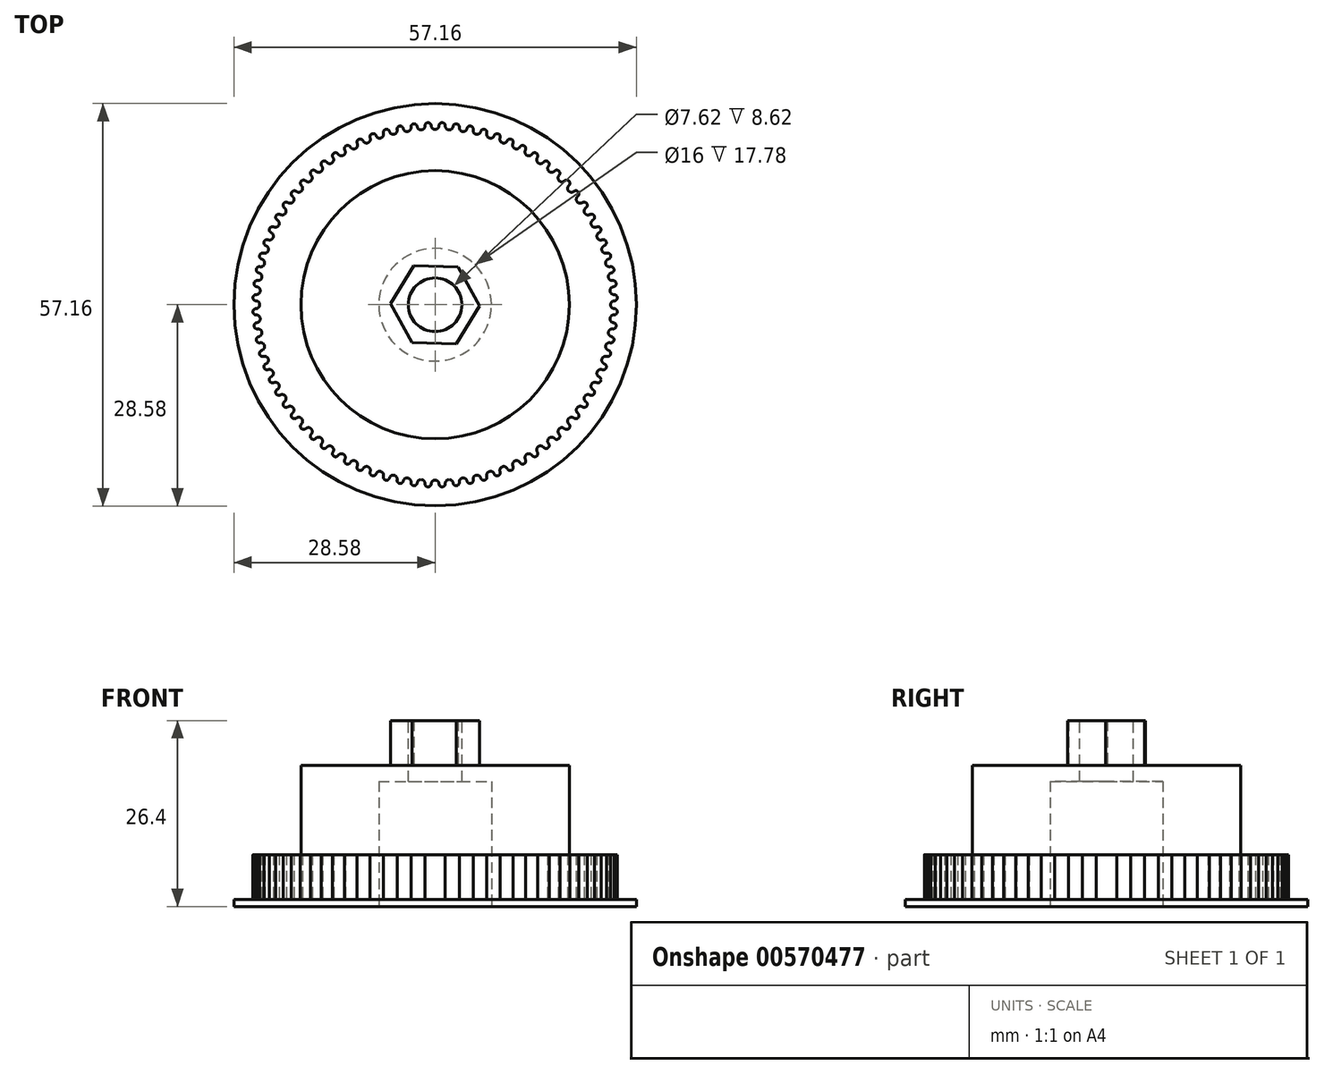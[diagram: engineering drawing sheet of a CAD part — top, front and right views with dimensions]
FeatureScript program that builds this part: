
annotation { "Feature Type Name" : "Feature", "Feature Type Description" : "" }
export const myFeature = defineFeature(function(context is Context, id is Id, definition is map)
    precondition{}
    {
        {
            var Q0;
            Q0=qCreatedBy(makeId("Top.planeOp"),FACE);
            var sketch = newSketch(context, id + "F0", { "sketchPlane" : qUnion([Q0])});
            skCircle(sketch, "E0", {"center": v(0, 0) * mm, "radius": 28.58 * mm});
            skSolve(sketch);
        }
        {
            var Q0;
            Q0 = qSketchRegion(id + "F0", true);
            extrude(context, id + "F1", {"entities" : qUnion([Q0]), "depth" : 1 * mm, "offsetDistance" : 25.4 * mm});
        }
        {
            var Q0;
            Q0=makeQuery(id+"F1.opExtrude","CAP_FACE",FACE,{"disambiguationData":[OSD([sQuery(id+"F0.wireOp",EDGE,"E0")])],"isStart":false});
            var sketch = newSketch(context, id + "F2", { "sketchPlane" : qUnion([Q0])});
            skArc(sketch, "E1", {"start": v(0, 24.9) * mm, "mid": v(-0.98, -24.89) * mm, "end": v(1.95, 24.83) * mm, "construction": true});
            skArc(sketch, "E2", {"start": v(0, 24.9) * mm, "mid": v(0.4, 25.07) * mm, "end": v(0.55, 25.46) * mm});
            skArc(sketch, "E3", {"start": v(1.44, 25.42) * mm, "mid": v(1.58, 25.02) * mm, "end": v(1.95, 24.83) * mm});
            skLineSegment(sketch, "E4", {"start": v(1.95, 24.83) * mm, "end": v(0, 0) * mm, "construction": true});
            skArc(sketch, "E5", {"start": v(1.44, 25.4) * mm, "mid": v(1.02, 25.87) * mm, "end": v(0.55, 25.44) * mm});
            skArc(sketch, "E6.1.0", {"start": v(-0.55, 25.44) * mm, "mid": v(-1.02, 25.87) * mm, "end": v(-1.44, 25.4) * mm});
            skArc(sketch, "E6.1.1", {"start": v(-1.95, 24.83) * mm, "mid": v(-1.58, 25.02) * mm, "end": v(-1.44, 25.42) * mm});
            skArc(sketch, "E6.1.2", {"start": v(-0.55, 25.46) * mm, "mid": v(-0.4, 25.07) * mm, "end": v(0, 24.9) * mm});
            skArc(sketch, "E6.2.0", {"start": v(-2.55, 25.32) * mm, "mid": v(-3.04, 25.7) * mm, "end": v(-3.43, 25.22) * mm});
            skArc(sketch, "E6.2.1", {"start": v(-3.9, 24.6) * mm, "mid": v(-3.54, 24.82) * mm, "end": v(-3.43, 25.23) * mm});
            skArc(sketch, "E6.2.2", {"start": v(-2.55, 25.34) * mm, "mid": v(-2.36, 24.96) * mm, "end": v(-1.95, 24.83) * mm});
            skArc(sketch, "E6.3.0", {"start": v(-4.53, 25.04) * mm, "mid": v(-5.05, 25.4) * mm, "end": v(-5.4, 24.87) * mm});
            skArc(sketch, "E6.3.1", {"start": v(-5.81, 24.22) * mm, "mid": v(-5.47, 24.47) * mm, "end": v(-5.4, 24.88) * mm});
            skArc(sketch, "E6.3.2", {"start": v(-4.53, 25.06) * mm, "mid": v(-4.3, 24.7) * mm, "end": v(-3.9, 24.6) * mm});
            skArc(sketch, "E6.4.0", {"start": v(-6.48, 24.6) * mm, "mid": v(-7.03, 24.92) * mm, "end": v(-7.33, 24.37) * mm});
            skArc(sketch, "E6.4.1", {"start": v(-7.7, 23.69) * mm, "mid": v(-7.38, 23.96) * mm, "end": v(-7.34, 24.38) * mm});
            skArc(sketch, "E6.4.2", {"start": v(-6.48, 24.62) * mm, "mid": v(-6.23, 24.29) * mm, "end": v(-5.81, 24.22) * mm});
            skArc(sketch, "E6.5.0", {"start": v(-8.39, 24.03) * mm, "mid": v(-8.96, 24.29) * mm, "end": v(-9.22, 23.72) * mm});
            skArc(sketch, "E6.5.1", {"start": v(-9.53, 23.01) * mm, "mid": v(-9.23, 23.31) * mm, "end": v(-9.23, 23.73) * mm});
            skArc(sketch, "E6.5.2", {"start": v(-8.4, 24.04) * mm, "mid": v(-8.12, 23.72) * mm, "end": v(-7.7, 23.69) * mm});
            skArc(sketch, "E6.6.0", {"start": v(-10.25, 23.3) * mm, "mid": v(-10.84, 23.51) * mm, "end": v(-11.06, 22.92) * mm});
            skArc(sketch, "E6.6.1", {"start": v(-11.3, 22.2) * mm, "mid": v(-11.03, 22.51) * mm, "end": v(-11.06, 22.93) * mm});
            skArc(sketch, "E6.6.2", {"start": v(-10.25, 23.3) * mm, "mid": v(-9.95, 23.01) * mm, "end": v(-9.53, 23.01) * mm});
            skArc(sketch, "E6.7.0", {"start": v(-12.04, 22.42) * mm, "mid": v(-12.65, 22.59) * mm, "end": v(-12.82, 21.98) * mm});
            skArc(sketch, "E6.7.1", {"start": v(-13.01, 21.24) * mm, "mid": v(-12.77, 21.58) * mm, "end": v(-12.83, 22) * mm});
            skArc(sketch, "E6.7.2", {"start": v(-12.05, 22.43) * mm, "mid": v(-11.73, 22.16) * mm, "end": v(-11.3, 22.2) * mm});
            skArc(sketch, "E6.8.0", {"start": v(-13.77, 21.4) * mm, "mid": v(-14.38, 21.53) * mm, "end": v(-14.5, 20.9) * mm});
            skArc(sketch, "E6.8.1", {"start": v(-14.64, 20.15) * mm, "mid": v(-14.42, 20.51) * mm, "end": v(-14.51, 20.92) * mm});
            skArc(sketch, "E6.8.2", {"start": v(-13.77, 21.42) * mm, "mid": v(-13.43, 21.17) * mm, "end": v(-13.01, 21.24) * mm});
            skArc(sketch, "E6.9.0", {"start": v(-15.4, 20.26) * mm, "mid": v(-16.03, 20.33) * mm, "end": v(-16.1, 19.7) * mm});
            skArc(sketch, "E6.9.1", {"start": v(-16.18, 18.94) * mm, "mid": v(-15.98, 19.32) * mm, "end": v(-16.11, 19.72) * mm});
            skArc(sketch, "E6.9.2", {"start": v(-15.41, 20.27) * mm, "mid": v(-15.05, 20.05) * mm, "end": v(-14.64, 20.15) * mm});
            skArc(sketch, "E6.10.0", {"start": v(-16.94, 18.99) * mm, "mid": v(-17.57, 19.01) * mm, "end": v(-17.6, 18.38) * mm});
            skArc(sketch, "E6.10.1", {"start": v(-17.61, 17.61) * mm, "mid": v(-17.45, 18) * mm, "end": v(-17.6, 18.4) * mm});
            skArc(sketch, "E6.10.2", {"start": v(-16.96, 19) * mm, "mid": v(-16.58, 18.8) * mm, "end": v(-16.18, 18.94) * mm});
            skArc(sketch, "E6.11.0", {"start": v(-18.38, 17.6) * mm, "mid": v(-19.01, 17.57) * mm, "end": v(-18.99, 16.94) * mm});
            skArc(sketch, "E6.11.1", {"start": v(-18.94, 16.18) * mm, "mid": v(-18.8, 16.58) * mm, "end": v(-19, 16.96) * mm});
            skArc(sketch, "E6.11.2", {"start": v(-18.4, 17.6) * mm, "mid": v(-18, 17.45) * mm, "end": v(-17.61, 17.61) * mm});
            skArc(sketch, "E6.12.0", {"start": v(-19.7, 16.1) * mm, "mid": v(-20.33, 16.03) * mm, "end": v(-20.26, 15.4) * mm});
            skArc(sketch, "E6.12.1", {"start": v(-20.15, 14.64) * mm, "mid": v(-20.05, 15.05) * mm, "end": v(-20.27, 15.41) * mm});
            skArc(sketch, "E6.12.2", {"start": v(-19.72, 16.11) * mm, "mid": v(-19.32, 15.98) * mm, "end": v(-18.94, 16.18) * mm});
            skArc(sketch, "E6.13.0", {"start": v(-20.9, 14.5) * mm, "mid": v(-21.53, 14.38) * mm, "end": v(-21.4, 13.77) * mm});
            skArc(sketch, "E6.13.1", {"start": v(-21.24, 13.01) * mm, "mid": v(-21.17, 13.43) * mm, "end": v(-21.42, 13.77) * mm});
            skArc(sketch, "E6.13.2", {"start": v(-20.92, 14.51) * mm, "mid": v(-20.51, 14.42) * mm, "end": v(-20.15, 14.64) * mm});
            skArc(sketch, "E6.14.0", {"start": v(-21.98, 12.82) * mm, "mid": v(-22.59, 12.65) * mm, "end": v(-22.42, 12.04) * mm});
            skArc(sketch, "E6.14.1", {"start": v(-22.2, 11.3) * mm, "mid": v(-22.16, 11.73) * mm, "end": v(-22.43, 12.05) * mm});
            skArc(sketch, "E6.14.2", {"start": v(-22, 12.83) * mm, "mid": v(-21.58, 12.77) * mm, "end": v(-21.24, 13.01) * mm});
            skArc(sketch, "E6.15.0", {"start": v(-22.92, 11.06) * mm, "mid": v(-23.51, 10.84) * mm, "end": v(-23.3, 10.25) * mm});
            skArc(sketch, "E6.15.1", {"start": v(-23.01, 9.53) * mm, "mid": v(-23.01, 9.95) * mm, "end": v(-23.3, 10.25) * mm});
            skArc(sketch, "E6.15.2", {"start": v(-22.93, 11.06) * mm, "mid": v(-22.51, 11.03) * mm, "end": v(-22.2, 11.3) * mm});
            skArc(sketch, "E6.16.0", {"start": v(-23.72, 9.22) * mm, "mid": v(-24.29, 8.96) * mm, "end": v(-24.03, 8.39) * mm});
            skArc(sketch, "E6.16.1", {"start": v(-23.69, 7.7) * mm, "mid": v(-23.72, 8.12) * mm, "end": v(-24.04, 8.4) * mm});
            skArc(sketch, "E6.16.2", {"start": v(-23.73, 9.23) * mm, "mid": v(-23.31, 9.23) * mm, "end": v(-23.01, 9.53) * mm});
            skArc(sketch, "E6.17.0", {"start": v(-24.37, 7.33) * mm, "mid": v(-24.92, 7.03) * mm, "end": v(-24.6, 6.48) * mm});
            skArc(sketch, "E6.17.1", {"start": v(-24.22, 5.81) * mm, "mid": v(-24.29, 6.23) * mm, "end": v(-24.62, 6.48) * mm});
            skArc(sketch, "E6.17.2", {"start": v(-24.38, 7.34) * mm, "mid": v(-23.96, 7.38) * mm, "end": v(-23.69, 7.7) * mm});
            skArc(sketch, "E6.18.0", {"start": v(-24.87, 5.4) * mm, "mid": v(-25.4, 5.05) * mm, "end": v(-25.04, 4.53) * mm});
            skArc(sketch, "E6.18.1", {"start": v(-24.6, 3.9) * mm, "mid": v(-24.7, 4.3) * mm, "end": v(-25.06, 4.53) * mm});
            skArc(sketch, "E6.18.2", {"start": v(-24.88, 5.4) * mm, "mid": v(-24.47, 5.47) * mm, "end": v(-24.22, 5.81) * mm});
            skArc(sketch, "E6.19.0", {"start": v(-25.22, 3.43) * mm, "mid": v(-25.7, 3.04) * mm, "end": v(-25.32, 2.55) * mm});
            skArc(sketch, "E6.19.1", {"start": v(-24.83, 1.95) * mm, "mid": v(-24.96, 2.36) * mm, "end": v(-25.34, 2.55) * mm});
            skArc(sketch, "E6.19.2", {"start": v(-25.23, 3.43) * mm, "mid": v(-24.82, 3.54) * mm, "end": v(-24.6, 3.9) * mm});
            skArc(sketch, "E6.20.0", {"start": v(-25.4, 1.44) * mm, "mid": v(-25.87, 1.02) * mm, "end": v(-25.44, 0.55) * mm});
            skArc(sketch, "E6.20.1", {"start": v(-24.9, 0) * mm, "mid": v(-25.07, 0.4) * mm, "end": v(-25.46, 0.55) * mm});
            skArc(sketch, "E6.20.2", {"start": v(-25.42, 1.44) * mm, "mid": v(-25.02, 1.58) * mm, "end": v(-24.83, 1.95) * mm});
            skArc(sketch, "E6.21.0", {"start": v(-25.44, -0.55) * mm, "mid": v(-25.87, -1.02) * mm, "end": v(-25.4, -1.44) * mm});
            skArc(sketch, "E6.21.1", {"start": v(-24.83, -1.95) * mm, "mid": v(-25.02, -1.58) * mm, "end": v(-25.42, -1.44) * mm});
            skArc(sketch, "E6.21.2", {"start": v(-25.46, -0.55) * mm, "mid": v(-25.07, -0.4) * mm, "end": v(-24.9, 0) * mm});
            skArc(sketch, "E6.22.0", {"start": v(-25.32, -2.55) * mm, "mid": v(-25.7, -3.04) * mm, "end": v(-25.22, -3.43) * mm});
            skArc(sketch, "E6.22.1", {"start": v(-24.6, -3.9) * mm, "mid": v(-24.82, -3.54) * mm, "end": v(-25.23, -3.43) * mm});
            skArc(sketch, "E6.22.2", {"start": v(-25.34, -2.55) * mm, "mid": v(-24.96, -2.36) * mm, "end": v(-24.83, -1.95) * mm});
            skArc(sketch, "E6.23.0", {"start": v(-25.04, -4.53) * mm, "mid": v(-25.4, -5.05) * mm, "end": v(-24.87, -5.4) * mm});
            skArc(sketch, "E6.23.1", {"start": v(-24.22, -5.81) * mm, "mid": v(-24.47, -5.47) * mm, "end": v(-24.88, -5.4) * mm});
            skArc(sketch, "E6.23.2", {"start": v(-25.06, -4.53) * mm, "mid": v(-24.7, -4.3) * mm, "end": v(-24.6, -3.9) * mm});
            skArc(sketch, "E6.24.0", {"start": v(-24.6, -6.48) * mm, "mid": v(-24.92, -7.03) * mm, "end": v(-24.37, -7.33) * mm});
            skArc(sketch, "E6.24.1", {"start": v(-23.69, -7.7) * mm, "mid": v(-23.96, -7.38) * mm, "end": v(-24.38, -7.34) * mm});
            skArc(sketch, "E6.24.2", {"start": v(-24.62, -6.48) * mm, "mid": v(-24.29, -6.23) * mm, "end": v(-24.22, -5.81) * mm});
            skArc(sketch, "E6.25.0", {"start": v(-24.03, -8.39) * mm, "mid": v(-24.29, -8.96) * mm, "end": v(-23.72, -9.22) * mm});
            skArc(sketch, "E6.25.1", {"start": v(-23.01, -9.53) * mm, "mid": v(-23.31, -9.23) * mm, "end": v(-23.73, -9.23) * mm});
            skArc(sketch, "E6.25.2", {"start": v(-24.04, -8.4) * mm, "mid": v(-23.72, -8.12) * mm, "end": v(-23.69, -7.7) * mm});
            skArc(sketch, "E6.26.0", {"start": v(-23.3, -10.25) * mm, "mid": v(-23.51, -10.84) * mm, "end": v(-22.92, -11.06) * mm});
            skArc(sketch, "E6.26.1", {"start": v(-22.2, -11.3) * mm, "mid": v(-22.51, -11.03) * mm, "end": v(-22.93, -11.06) * mm});
            skArc(sketch, "E6.26.2", {"start": v(-23.3, -10.25) * mm, "mid": v(-23.01, -9.95) * mm, "end": v(-23.01, -9.53) * mm});
            skArc(sketch, "E6.27.0", {"start": v(-22.42, -12.04) * mm, "mid": v(-22.59, -12.65) * mm, "end": v(-21.98, -12.82) * mm});
            skArc(sketch, "E6.27.1", {"start": v(-21.24, -13.01) * mm, "mid": v(-21.58, -12.77) * mm, "end": v(-22, -12.83) * mm});
            skArc(sketch, "E6.27.2", {"start": v(-22.43, -12.05) * mm, "mid": v(-22.16, -11.73) * mm, "end": v(-22.2, -11.3) * mm});
            skArc(sketch, "E6.28.0", {"start": v(-21.4, -13.77) * mm, "mid": v(-21.53, -14.38) * mm, "end": v(-20.9, -14.5) * mm});
            skArc(sketch, "E6.28.1", {"start": v(-20.15, -14.64) * mm, "mid": v(-20.51, -14.42) * mm, "end": v(-20.92, -14.51) * mm});
            skArc(sketch, "E6.28.2", {"start": v(-21.42, -13.77) * mm, "mid": v(-21.17, -13.43) * mm, "end": v(-21.24, -13.01) * mm});
            skArc(sketch, "E6.29.0", {"start": v(-20.26, -15.4) * mm, "mid": v(-20.33, -16.03) * mm, "end": v(-19.7, -16.1) * mm});
            skArc(sketch, "E6.29.1", {"start": v(-18.94, -16.18) * mm, "mid": v(-19.32, -15.98) * mm, "end": v(-19.72, -16.11) * mm});
            skArc(sketch, "E6.29.2", {"start": v(-20.27, -15.41) * mm, "mid": v(-20.05, -15.05) * mm, "end": v(-20.15, -14.64) * mm});
            skArc(sketch, "E6.30.0", {"start": v(-18.99, -16.94) * mm, "mid": v(-19.01, -17.57) * mm, "end": v(-18.38, -17.6) * mm});
            skArc(sketch, "E6.30.1", {"start": v(-17.61, -17.61) * mm, "mid": v(-18, -17.45) * mm, "end": v(-18.4, -17.6) * mm});
            skArc(sketch, "E6.30.2", {"start": v(-19, -16.96) * mm, "mid": v(-18.8, -16.58) * mm, "end": v(-18.94, -16.18) * mm});
            skArc(sketch, "E6.31.0", {"start": v(-17.6, -18.38) * mm, "mid": v(-17.57, -19.01) * mm, "end": v(-16.94, -18.99) * mm});
            skArc(sketch, "E6.31.1", {"start": v(-16.18, -18.94) * mm, "mid": v(-16.58, -18.8) * mm, "end": v(-16.96, -19) * mm});
            skArc(sketch, "E6.31.2", {"start": v(-17.6, -18.4) * mm, "mid": v(-17.45, -18) * mm, "end": v(-17.61, -17.61) * mm});
            skArc(sketch, "E6.32.0", {"start": v(-16.1, -19.7) * mm, "mid": v(-16.03, -20.33) * mm, "end": v(-15.4, -20.26) * mm});
            skArc(sketch, "E6.32.1", {"start": v(-14.64, -20.15) * mm, "mid": v(-15.05, -20.05) * mm, "end": v(-15.41, -20.27) * mm});
            skArc(sketch, "E6.32.2", {"start": v(-16.11, -19.72) * mm, "mid": v(-15.98, -19.32) * mm, "end": v(-16.18, -18.94) * mm});
            skArc(sketch, "E6.33.0", {"start": v(-14.5, -20.9) * mm, "mid": v(-14.38, -21.53) * mm, "end": v(-13.77, -21.4) * mm});
            skArc(sketch, "E6.33.1", {"start": v(-13.01, -21.24) * mm, "mid": v(-13.43, -21.17) * mm, "end": v(-13.77, -21.42) * mm});
            skArc(sketch, "E6.33.2", {"start": v(-14.51, -20.92) * mm, "mid": v(-14.42, -20.51) * mm, "end": v(-14.64, -20.15) * mm});
            skArc(sketch, "E6.34.0", {"start": v(-12.82, -21.98) * mm, "mid": v(-12.65, -22.59) * mm, "end": v(-12.04, -22.42) * mm});
            skArc(sketch, "E6.34.1", {"start": v(-11.3, -22.2) * mm, "mid": v(-11.73, -22.16) * mm, "end": v(-12.05, -22.43) * mm});
            skArc(sketch, "E6.34.2", {"start": v(-12.83, -22) * mm, "mid": v(-12.77, -21.58) * mm, "end": v(-13.01, -21.24) * mm});
            skArc(sketch, "E6.35.0", {"start": v(-11.06, -22.92) * mm, "mid": v(-10.84, -23.51) * mm, "end": v(-10.25, -23.3) * mm});
            skArc(sketch, "E6.35.1", {"start": v(-9.53, -23.01) * mm, "mid": v(-9.95, -23.01) * mm, "end": v(-10.25, -23.3) * mm});
            skArc(sketch, "E6.35.2", {"start": v(-11.06, -22.93) * mm, "mid": v(-11.03, -22.51) * mm, "end": v(-11.3, -22.2) * mm});
            skArc(sketch, "E6.36.0", {"start": v(-9.22, -23.72) * mm, "mid": v(-8.96, -24.29) * mm, "end": v(-8.39, -24.03) * mm});
            skArc(sketch, "E6.36.1", {"start": v(-7.7, -23.69) * mm, "mid": v(-8.12, -23.72) * mm, "end": v(-8.4, -24.04) * mm});
            skArc(sketch, "E6.36.2", {"start": v(-9.23, -23.73) * mm, "mid": v(-9.23, -23.31) * mm, "end": v(-9.53, -23.01) * mm});
            skArc(sketch, "E6.37.0", {"start": v(-7.33, -24.37) * mm, "mid": v(-7.03, -24.92) * mm, "end": v(-6.48, -24.6) * mm});
            skArc(sketch, "E6.37.1", {"start": v(-5.81, -24.22) * mm, "mid": v(-6.23, -24.29) * mm, "end": v(-6.48, -24.62) * mm});
            skArc(sketch, "E6.37.2", {"start": v(-7.34, -24.38) * mm, "mid": v(-7.38, -23.96) * mm, "end": v(-7.7, -23.69) * mm});
            skArc(sketch, "E6.38.0", {"start": v(-5.4, -24.87) * mm, "mid": v(-5.05, -25.4) * mm, "end": v(-4.53, -25.04) * mm});
            skArc(sketch, "E6.38.1", {"start": v(-3.9, -24.6) * mm, "mid": v(-4.3, -24.7) * mm, "end": v(-4.53, -25.06) * mm});
            skArc(sketch, "E6.38.2", {"start": v(-5.4, -24.88) * mm, "mid": v(-5.47, -24.47) * mm, "end": v(-5.81, -24.22) * mm});
            skArc(sketch, "E6.39.0", {"start": v(-3.43, -25.22) * mm, "mid": v(-3.04, -25.7) * mm, "end": v(-2.55, -25.32) * mm});
            skArc(sketch, "E6.39.1", {"start": v(-1.95, -24.83) * mm, "mid": v(-2.36, -24.96) * mm, "end": v(-2.55, -25.34) * mm});
            skArc(sketch, "E6.39.2", {"start": v(-3.43, -25.23) * mm, "mid": v(-3.54, -24.82) * mm, "end": v(-3.9, -24.6) * mm});
            skArc(sketch, "E6.40.0", {"start": v(-1.44, -25.4) * mm, "mid": v(-1.02, -25.87) * mm, "end": v(-0.55, -25.44) * mm});
            skArc(sketch, "E6.40.1", {"start": v(0, -24.9) * mm, "mid": v(-0.4, -25.07) * mm, "end": v(-0.55, -25.46) * mm});
            skArc(sketch, "E6.40.2", {"start": v(-1.44, -25.42) * mm, "mid": v(-1.58, -25.02) * mm, "end": v(-1.95, -24.83) * mm});
            skArc(sketch, "E6.41.0", {"start": v(0.55, -25.44) * mm, "mid": v(1.02, -25.87) * mm, "end": v(1.44, -25.4) * mm});
            skArc(sketch, "E6.41.1", {"start": v(1.95, -24.83) * mm, "mid": v(1.58, -25.02) * mm, "end": v(1.44, -25.42) * mm});
            skArc(sketch, "E6.41.2", {"start": v(0.55, -25.46) * mm, "mid": v(0.4, -25.07) * mm, "end": v(0, -24.9) * mm});
            skArc(sketch, "E6.42.0", {"start": v(2.55, -25.32) * mm, "mid": v(3.04, -25.7) * mm, "end": v(3.43, -25.22) * mm});
            skArc(sketch, "E6.42.1", {"start": v(3.9, -24.6) * mm, "mid": v(3.54, -24.82) * mm, "end": v(3.43, -25.23) * mm});
            skArc(sketch, "E6.42.2", {"start": v(2.55, -25.34) * mm, "mid": v(2.36, -24.96) * mm, "end": v(1.95, -24.83) * mm});
            skArc(sketch, "E6.43.0", {"start": v(4.53, -25.04) * mm, "mid": v(5.05, -25.4) * mm, "end": v(5.4, -24.87) * mm});
            skArc(sketch, "E6.43.1", {"start": v(5.81, -24.22) * mm, "mid": v(5.47, -24.47) * mm, "end": v(5.4, -24.88) * mm});
            skArc(sketch, "E6.43.2", {"start": v(4.53, -25.06) * mm, "mid": v(4.3, -24.7) * mm, "end": v(3.9, -24.6) * mm});
            skArc(sketch, "E6.44.0", {"start": v(6.48, -24.6) * mm, "mid": v(7.03, -24.92) * mm, "end": v(7.33, -24.37) * mm});
            skArc(sketch, "E6.44.1", {"start": v(7.7, -23.69) * mm, "mid": v(7.38, -23.96) * mm, "end": v(7.34, -24.38) * mm});
            skArc(sketch, "E6.44.2", {"start": v(6.48, -24.62) * mm, "mid": v(6.23, -24.29) * mm, "end": v(5.81, -24.22) * mm});
            skArc(sketch, "E6.45.0", {"start": v(8.39, -24.03) * mm, "mid": v(8.96, -24.29) * mm, "end": v(9.22, -23.72) * mm});
            skArc(sketch, "E6.45.1", {"start": v(9.53, -23.01) * mm, "mid": v(9.23, -23.31) * mm, "end": v(9.23, -23.73) * mm});
            skArc(sketch, "E6.45.2", {"start": v(8.4, -24.04) * mm, "mid": v(8.12, -23.72) * mm, "end": v(7.7, -23.69) * mm});
            skArc(sketch, "E6.46.0", {"start": v(10.25, -23.3) * mm, "mid": v(10.84, -23.51) * mm, "end": v(11.06, -22.92) * mm});
            skArc(sketch, "E6.46.1", {"start": v(11.3, -22.2) * mm, "mid": v(11.03, -22.51) * mm, "end": v(11.06, -22.93) * mm});
            skArc(sketch, "E6.46.2", {"start": v(10.25, -23.3) * mm, "mid": v(9.95, -23.01) * mm, "end": v(9.53, -23.01) * mm});
            skArc(sketch, "E6.47.0", {"start": v(12.04, -22.42) * mm, "mid": v(12.65, -22.59) * mm, "end": v(12.82, -21.98) * mm});
            skArc(sketch, "E6.47.1", {"start": v(13.01, -21.24) * mm, "mid": v(12.77, -21.58) * mm, "end": v(12.83, -22) * mm});
            skArc(sketch, "E6.47.2", {"start": v(12.05, -22.43) * mm, "mid": v(11.73, -22.16) * mm, "end": v(11.3, -22.2) * mm});
            skArc(sketch, "E6.48.0", {"start": v(13.77, -21.4) * mm, "mid": v(14.38, -21.53) * mm, "end": v(14.5, -20.9) * mm});
            skArc(sketch, "E6.48.1", {"start": v(14.64, -20.15) * mm, "mid": v(14.42, -20.51) * mm, "end": v(14.51, -20.92) * mm});
            skArc(sketch, "E6.48.2", {"start": v(13.77, -21.42) * mm, "mid": v(13.43, -21.17) * mm, "end": v(13.01, -21.24) * mm});
            skArc(sketch, "E6.49.0", {"start": v(15.4, -20.26) * mm, "mid": v(16.03, -20.33) * mm, "end": v(16.1, -19.7) * mm});
            skArc(sketch, "E6.49.1", {"start": v(16.18, -18.94) * mm, "mid": v(15.98, -19.32) * mm, "end": v(16.11, -19.72) * mm});
            skArc(sketch, "E6.49.2", {"start": v(15.41, -20.27) * mm, "mid": v(15.05, -20.05) * mm, "end": v(14.64, -20.15) * mm});
            skArc(sketch, "E6.50.0", {"start": v(16.94, -18.99) * mm, "mid": v(17.57, -19.01) * mm, "end": v(17.6, -18.38) * mm});
            skArc(sketch, "E6.50.1", {"start": v(17.61, -17.61) * mm, "mid": v(17.45, -18) * mm, "end": v(17.6, -18.4) * mm});
            skArc(sketch, "E6.50.2", {"start": v(16.96, -19) * mm, "mid": v(16.58, -18.8) * mm, "end": v(16.18, -18.94) * mm});
            skArc(sketch, "E6.51.0", {"start": v(18.38, -17.6) * mm, "mid": v(19.01, -17.57) * mm, "end": v(18.99, -16.94) * mm});
            skArc(sketch, "E6.51.1", {"start": v(18.94, -16.18) * mm, "mid": v(18.8, -16.58) * mm, "end": v(19, -16.96) * mm});
            skArc(sketch, "E6.51.2", {"start": v(18.4, -17.6) * mm, "mid": v(18, -17.45) * mm, "end": v(17.61, -17.61) * mm});
            skArc(sketch, "E6.52.0", {"start": v(19.7, -16.1) * mm, "mid": v(20.33, -16.03) * mm, "end": v(20.26, -15.4) * mm});
            skArc(sketch, "E6.52.1", {"start": v(20.15, -14.64) * mm, "mid": v(20.05, -15.05) * mm, "end": v(20.27, -15.41) * mm});
            skArc(sketch, "E6.52.2", {"start": v(19.72, -16.11) * mm, "mid": v(19.32, -15.98) * mm, "end": v(18.94, -16.18) * mm});
            skArc(sketch, "E6.53.0", {"start": v(20.9, -14.5) * mm, "mid": v(21.53, -14.38) * mm, "end": v(21.4, -13.77) * mm});
            skArc(sketch, "E6.53.1", {"start": v(21.24, -13.01) * mm, "mid": v(21.17, -13.43) * mm, "end": v(21.42, -13.77) * mm});
            skArc(sketch, "E6.53.2", {"start": v(20.92, -14.51) * mm, "mid": v(20.51, -14.42) * mm, "end": v(20.15, -14.64) * mm});
            skArc(sketch, "E6.54.0", {"start": v(21.98, -12.82) * mm, "mid": v(22.59, -12.65) * mm, "end": v(22.42, -12.04) * mm});
            skArc(sketch, "E6.54.1", {"start": v(22.2, -11.3) * mm, "mid": v(22.16, -11.73) * mm, "end": v(22.43, -12.05) * mm});
            skArc(sketch, "E6.54.2", {"start": v(22, -12.83) * mm, "mid": v(21.58, -12.77) * mm, "end": v(21.24, -13.01) * mm});
            skArc(sketch, "E6.55.0", {"start": v(22.92, -11.06) * mm, "mid": v(23.51, -10.84) * mm, "end": v(23.3, -10.25) * mm});
            skArc(sketch, "E6.55.1", {"start": v(23.01, -9.53) * mm, "mid": v(23.01, -9.95) * mm, "end": v(23.3, -10.25) * mm});
            skArc(sketch, "E6.55.2", {"start": v(22.93, -11.06) * mm, "mid": v(22.51, -11.03) * mm, "end": v(22.2, -11.3) * mm});
            skArc(sketch, "E6.56.0", {"start": v(23.72, -9.22) * mm, "mid": v(24.29, -8.96) * mm, "end": v(24.03, -8.39) * mm});
            skArc(sketch, "E6.56.1", {"start": v(23.69, -7.7) * mm, "mid": v(23.72, -8.12) * mm, "end": v(24.04, -8.4) * mm});
            skArc(sketch, "E6.56.2", {"start": v(23.73, -9.23) * mm, "mid": v(23.31, -9.23) * mm, "end": v(23.01, -9.53) * mm});
            skArc(sketch, "E6.57.0", {"start": v(24.37, -7.33) * mm, "mid": v(24.92, -7.03) * mm, "end": v(24.6, -6.48) * mm});
            skArc(sketch, "E6.57.1", {"start": v(24.22, -5.81) * mm, "mid": v(24.29, -6.23) * mm, "end": v(24.62, -6.48) * mm});
            skArc(sketch, "E6.57.2", {"start": v(24.38, -7.34) * mm, "mid": v(23.96, -7.38) * mm, "end": v(23.69, -7.7) * mm});
            skArc(sketch, "E6.58.0", {"start": v(24.87, -5.4) * mm, "mid": v(25.4, -5.05) * mm, "end": v(25.04, -4.53) * mm});
            skArc(sketch, "E6.58.1", {"start": v(24.6, -3.9) * mm, "mid": v(24.7, -4.3) * mm, "end": v(25.06, -4.53) * mm});
            skArc(sketch, "E6.58.2", {"start": v(24.88, -5.4) * mm, "mid": v(24.47, -5.47) * mm, "end": v(24.22, -5.81) * mm});
            skArc(sketch, "E6.59.0", {"start": v(25.22, -3.43) * mm, "mid": v(25.7, -3.04) * mm, "end": v(25.32, -2.55) * mm});
            skArc(sketch, "E6.59.1", {"start": v(24.83, -1.95) * mm, "mid": v(24.96, -2.36) * mm, "end": v(25.34, -2.55) * mm});
            skArc(sketch, "E6.59.2", {"start": v(25.23, -3.43) * mm, "mid": v(24.82, -3.54) * mm, "end": v(24.6, -3.9) * mm});
            skArc(sketch, "E6.60.0", {"start": v(25.4, -1.44) * mm, "mid": v(25.87, -1.02) * mm, "end": v(25.44, -0.55) * mm});
            skArc(sketch, "E6.60.1", {"start": v(24.9, 0) * mm, "mid": v(25.07, -0.4) * mm, "end": v(25.46, -0.55) * mm});
            skArc(sketch, "E6.60.2", {"start": v(25.42, -1.44) * mm, "mid": v(25.02, -1.58) * mm, "end": v(24.83, -1.95) * mm});
            skArc(sketch, "E6.61.0", {"start": v(25.44, 0.55) * mm, "mid": v(25.87, 1.02) * mm, "end": v(25.4, 1.44) * mm});
            skArc(sketch, "E6.61.1", {"start": v(24.83, 1.95) * mm, "mid": v(25.02, 1.58) * mm, "end": v(25.42, 1.44) * mm});
            skArc(sketch, "E6.61.2", {"start": v(25.46, 0.55) * mm, "mid": v(25.07, 0.4) * mm, "end": v(24.9, 0) * mm});
            skArc(sketch, "E6.62.0", {"start": v(25.32, 2.55) * mm, "mid": v(25.7, 3.04) * mm, "end": v(25.22, 3.43) * mm});
            skArc(sketch, "E6.62.1", {"start": v(24.6, 3.9) * mm, "mid": v(24.82, 3.54) * mm, "end": v(25.23, 3.43) * mm});
            skArc(sketch, "E6.62.2", {"start": v(25.34, 2.55) * mm, "mid": v(24.96, 2.36) * mm, "end": v(24.83, 1.95) * mm});
            skArc(sketch, "E6.63.0", {"start": v(25.04, 4.53) * mm, "mid": v(25.4, 5.05) * mm, "end": v(24.87, 5.4) * mm});
            skArc(sketch, "E6.63.1", {"start": v(24.22, 5.81) * mm, "mid": v(24.47, 5.47) * mm, "end": v(24.88, 5.4) * mm});
            skArc(sketch, "E6.63.2", {"start": v(25.06, 4.53) * mm, "mid": v(24.7, 4.3) * mm, "end": v(24.6, 3.9) * mm});
            skArc(sketch, "E6.64.0", {"start": v(24.6, 6.48) * mm, "mid": v(24.92, 7.03) * mm, "end": v(24.37, 7.33) * mm});
            skArc(sketch, "E6.64.1", {"start": v(23.69, 7.7) * mm, "mid": v(23.96, 7.38) * mm, "end": v(24.38, 7.34) * mm});
            skArc(sketch, "E6.64.2", {"start": v(24.62, 6.48) * mm, "mid": v(24.29, 6.23) * mm, "end": v(24.22, 5.81) * mm});
            skArc(sketch, "E6.65.0", {"start": v(24.03, 8.39) * mm, "mid": v(24.29, 8.96) * mm, "end": v(23.72, 9.22) * mm});
            skArc(sketch, "E6.65.1", {"start": v(23.01, 9.53) * mm, "mid": v(23.31, 9.23) * mm, "end": v(23.73, 9.23) * mm});
            skArc(sketch, "E6.65.2", {"start": v(24.04, 8.4) * mm, "mid": v(23.72, 8.12) * mm, "end": v(23.69, 7.7) * mm});
            skArc(sketch, "E6.66.0", {"start": v(23.3, 10.25) * mm, "mid": v(23.51, 10.84) * mm, "end": v(22.92, 11.06) * mm});
            skArc(sketch, "E6.66.1", {"start": v(22.2, 11.3) * mm, "mid": v(22.51, 11.03) * mm, "end": v(22.93, 11.06) * mm});
            skArc(sketch, "E6.66.2", {"start": v(23.3, 10.25) * mm, "mid": v(23.01, 9.95) * mm, "end": v(23.01, 9.53) * mm});
            skArc(sketch, "E6.67.0", {"start": v(22.42, 12.04) * mm, "mid": v(22.59, 12.65) * mm, "end": v(21.98, 12.82) * mm});
            skArc(sketch, "E6.67.1", {"start": v(21.24, 13.01) * mm, "mid": v(21.58, 12.77) * mm, "end": v(22, 12.83) * mm});
            skArc(sketch, "E6.67.2", {"start": v(22.43, 12.05) * mm, "mid": v(22.16, 11.73) * mm, "end": v(22.2, 11.3) * mm});
            skArc(sketch, "E6.68.0", {"start": v(21.4, 13.77) * mm, "mid": v(21.53, 14.38) * mm, "end": v(20.9, 14.5) * mm});
            skArc(sketch, "E6.68.1", {"start": v(20.15, 14.64) * mm, "mid": v(20.51, 14.42) * mm, "end": v(20.92, 14.51) * mm});
            skArc(sketch, "E6.68.2", {"start": v(21.42, 13.77) * mm, "mid": v(21.17, 13.43) * mm, "end": v(21.24, 13.01) * mm});
            skArc(sketch, "E6.69.0", {"start": v(20.26, 15.4) * mm, "mid": v(20.33, 16.03) * mm, "end": v(19.7, 16.1) * mm});
            skArc(sketch, "E6.69.1", {"start": v(18.94, 16.18) * mm, "mid": v(19.32, 15.98) * mm, "end": v(19.72, 16.11) * mm});
            skArc(sketch, "E6.69.2", {"start": v(20.27, 15.41) * mm, "mid": v(20.05, 15.05) * mm, "end": v(20.15, 14.64) * mm});
            skArc(sketch, "E6.70.0", {"start": v(18.99, 16.94) * mm, "mid": v(19.01, 17.57) * mm, "end": v(18.38, 17.6) * mm});
            skArc(sketch, "E6.70.1", {"start": v(17.61, 17.61) * mm, "mid": v(18, 17.45) * mm, "end": v(18.4, 17.6) * mm});
            skArc(sketch, "E6.70.2", {"start": v(19, 16.96) * mm, "mid": v(18.8, 16.58) * mm, "end": v(18.94, 16.18) * mm});
            skArc(sketch, "E6.71.0", {"start": v(17.6, 18.38) * mm, "mid": v(17.57, 19.01) * mm, "end": v(16.94, 18.99) * mm});
            skArc(sketch, "E6.71.1", {"start": v(16.18, 18.94) * mm, "mid": v(16.58, 18.8) * mm, "end": v(16.96, 19) * mm});
            skArc(sketch, "E6.71.2", {"start": v(17.6, 18.4) * mm, "mid": v(17.45, 18) * mm, "end": v(17.61, 17.61) * mm});
            skArc(sketch, "E6.72.0", {"start": v(16.1, 19.7) * mm, "mid": v(16.03, 20.33) * mm, "end": v(15.4, 20.26) * mm});
            skArc(sketch, "E6.72.1", {"start": v(14.64, 20.15) * mm, "mid": v(15.05, 20.05) * mm, "end": v(15.41, 20.27) * mm});
            skArc(sketch, "E6.72.2", {"start": v(16.11, 19.72) * mm, "mid": v(15.98, 19.32) * mm, "end": v(16.18, 18.94) * mm});
            skArc(sketch, "E6.73.0", {"start": v(14.5, 20.9) * mm, "mid": v(14.38, 21.53) * mm, "end": v(13.77, 21.4) * mm});
            skArc(sketch, "E6.73.1", {"start": v(13.01, 21.24) * mm, "mid": v(13.43, 21.17) * mm, "end": v(13.77, 21.42) * mm});
            skArc(sketch, "E6.73.2", {"start": v(14.51, 20.92) * mm, "mid": v(14.42, 20.51) * mm, "end": v(14.64, 20.15) * mm});
            skArc(sketch, "E6.74.0", {"start": v(12.82, 21.98) * mm, "mid": v(12.65, 22.59) * mm, "end": v(12.04, 22.42) * mm});
            skArc(sketch, "E6.74.1", {"start": v(11.3, 22.2) * mm, "mid": v(11.73, 22.16) * mm, "end": v(12.05, 22.43) * mm});
            skArc(sketch, "E6.74.2", {"start": v(12.83, 22) * mm, "mid": v(12.77, 21.58) * mm, "end": v(13.01, 21.24) * mm});
            skArc(sketch, "E6.75.0", {"start": v(11.06, 22.92) * mm, "mid": v(10.84, 23.51) * mm, "end": v(10.25, 23.3) * mm});
            skArc(sketch, "E6.75.1", {"start": v(9.53, 23.01) * mm, "mid": v(9.95, 23.01) * mm, "end": v(10.25, 23.3) * mm});
            skArc(sketch, "E6.75.2", {"start": v(11.06, 22.93) * mm, "mid": v(11.03, 22.51) * mm, "end": v(11.3, 22.2) * mm});
            skArc(sketch, "E6.76.0", {"start": v(9.22, 23.72) * mm, "mid": v(8.96, 24.29) * mm, "end": v(8.39, 24.03) * mm});
            skArc(sketch, "E6.76.1", {"start": v(7.7, 23.69) * mm, "mid": v(8.12, 23.72) * mm, "end": v(8.4, 24.04) * mm});
            skArc(sketch, "E6.76.2", {"start": v(9.23, 23.73) * mm, "mid": v(9.23, 23.31) * mm, "end": v(9.53, 23.01) * mm});
            skArc(sketch, "E6.77.0", {"start": v(7.33, 24.37) * mm, "mid": v(7.03, 24.92) * mm, "end": v(6.48, 24.6) * mm});
            skArc(sketch, "E6.77.1", {"start": v(5.81, 24.22) * mm, "mid": v(6.23, 24.29) * mm, "end": v(6.48, 24.62) * mm});
            skArc(sketch, "E6.77.2", {"start": v(7.34, 24.38) * mm, "mid": v(7.38, 23.96) * mm, "end": v(7.7, 23.69) * mm});
            skArc(sketch, "E6.78.0", {"start": v(5.4, 24.87) * mm, "mid": v(5.05, 25.4) * mm, "end": v(4.53, 25.04) * mm});
            skArc(sketch, "E6.78.1", {"start": v(3.9, 24.6) * mm, "mid": v(4.3, 24.7) * mm, "end": v(4.53, 25.06) * mm});
            skArc(sketch, "E6.78.2", {"start": v(5.4, 24.88) * mm, "mid": v(5.47, 24.47) * mm, "end": v(5.81, 24.22) * mm});
            skArc(sketch, "E6.79.0", {"start": v(3.43, 25.22) * mm, "mid": v(3.04, 25.7) * mm, "end": v(2.55, 25.32) * mm});
            skArc(sketch, "E6.79.1", {"start": v(1.95, 24.83) * mm, "mid": v(2.36, 24.96) * mm, "end": v(2.55, 25.34) * mm});
            skArc(sketch, "E6.79.2", {"start": v(3.43, 25.23) * mm, "mid": v(3.54, 24.82) * mm, "end": v(3.9, 24.6) * mm});
            skSolve(sketch);
        }
        {
            var Q0;
            {var subQ187=sQuery(id+"F2.wireOp",EDGE,"E5");Q0=makeQuery(id+"F2.imprint","IMPRINT",FACE,{"disambiguationData":[TD([[makeQuery(id+"F2.imprint","IMPRINT",EDGE,{"derivedFrom":subQ187}),1.0]])]});}
            extrude(context, id + "F3", {"entities" : qUnion([Q0]), "operationType" : NewBodyOperationType.ADD, "depth" : 6.35 * mm, "offsetDistance" : 25.4 * mm});
        }
        {
            var Q0;
            Q0=makeQuery(id+"F3.opExtrude","CAP_FACE",FACE,{"disambiguationData":[OSD([sQuery(id+"F2.wireOp",EDGE,"E2"),sQuery(id+"F2.wireOp",EDGE,"E3"),sQuery(id+"F2.wireOp",EDGE,"E5"),sQuery(id+"F2.wireOp",EDGE,"E6.1.0"),sQuery(id+"F2.wireOp",EDGE,"E6.1.1"),sQuery(id+"F2.wireOp",EDGE,"E6.1.2"),sQuery(id+"F2.wireOp",EDGE,"E6.2.0"),sQuery(id+"F2.wireOp",EDGE,"E6.2.1"),sQuery(id+"F2.wireOp",EDGE,"E6.2.2"),sQuery(id+"F2.wireOp",EDGE,"E6.3.0"),sQuery(id+"F2.wireOp",EDGE,"E6.3.1"),sQuery(id+"F2.wireOp",EDGE,"E6.3.2"),sQuery(id+"F2.wireOp",EDGE,"E6.4.0"),sQuery(id+"F2.wireOp",EDGE,"E6.4.1"),sQuery(id+"F2.wireOp",EDGE,"E6.4.2"),sQuery(id+"F2.wireOp",EDGE,"E6.5.0"),sQuery(id+"F2.wireOp",EDGE,"E6.5.1"),sQuery(id+"F2.wireOp",EDGE,"E6.5.2"),sQuery(id+"F2.wireOp",EDGE,"E6.6.0"),sQuery(id+"F2.wireOp",EDGE,"E6.6.1"),sQuery(id+"F2.wireOp",EDGE,"E6.6.2"),sQuery(id+"F2.wireOp",EDGE,"E6.7.0"),sQuery(id+"F2.wireOp",EDGE,"E6.7.1"),sQuery(id+"F2.wireOp",EDGE,"E6.7.2"),sQuery(id+"F2.wireOp",EDGE,"E6.8.0"),sQuery(id+"F2.wireOp",EDGE,"E6.8.1"),sQuery(id+"F2.wireOp",EDGE,"E6.8.2"),sQuery(id+"F2.wireOp",EDGE,"E6.9.0"),sQuery(id+"F2.wireOp",EDGE,"E6.9.1"),sQuery(id+"F2.wireOp",EDGE,"E6.9.2"),sQuery(id+"F2.wireOp",EDGE,"E6.10.0"),sQuery(id+"F2.wireOp",EDGE,"E6.10.1"),sQuery(id+"F2.wireOp",EDGE,"E6.10.2"),sQuery(id+"F2.wireOp",EDGE,"E6.11.0"),sQuery(id+"F2.wireOp",EDGE,"E6.11.1"),sQuery(id+"F2.wireOp",EDGE,"E6.11.2"),sQuery(id+"F2.wireOp",EDGE,"E6.12.0"),sQuery(id+"F2.wireOp",EDGE,"E6.12.1"),sQuery(id+"F2.wireOp",EDGE,"E6.12.2"),sQuery(id+"F2.wireOp",EDGE,"E6.13.0"),sQuery(id+"F2.wireOp",EDGE,"E6.13.1"),sQuery(id+"F2.wireOp",EDGE,"E6.13.2"),sQuery(id+"F2.wireOp",EDGE,"E6.14.0"),sQuery(id+"F2.wireOp",EDGE,"E6.14.1"),sQuery(id+"F2.wireOp",EDGE,"E6.14.2"),sQuery(id+"F2.wireOp",EDGE,"E6.15.0"),sQuery(id+"F2.wireOp",EDGE,"E6.15.1"),sQuery(id+"F2.wireOp",EDGE,"E6.15.2"),sQuery(id+"F2.wireOp",EDGE,"E6.16.0"),sQuery(id+"F2.wireOp",EDGE,"E6.16.1"),sQuery(id+"F2.wireOp",EDGE,"E6.16.2"),sQuery(id+"F2.wireOp",EDGE,"E6.17.0"),sQuery(id+"F2.wireOp",EDGE,"E6.17.1"),sQuery(id+"F2.wireOp",EDGE,"E6.17.2"),sQuery(id+"F2.wireOp",EDGE,"E6.18.0"),sQuery(id+"F2.wireOp",EDGE,"E6.18.1"),sQuery(id+"F2.wireOp",EDGE,"E6.18.2"),sQuery(id+"F2.wireOp",EDGE,"E6.19.0"),sQuery(id+"F2.wireOp",EDGE,"E6.19.1"),sQuery(id+"F2.wireOp",EDGE,"E6.19.2"),sQuery(id+"F2.wireOp",EDGE,"E6.20.0"),sQuery(id+"F2.wireOp",EDGE,"E6.20.1"),sQuery(id+"F2.wireOp",EDGE,"E6.20.2"),sQuery(id+"F2.wireOp",EDGE,"E6.21.0"),sQuery(id+"F2.wireOp",EDGE,"E6.21.1"),sQuery(id+"F2.wireOp",EDGE,"E6.21.2"),sQuery(id+"F2.wireOp",EDGE,"E6.22.0"),sQuery(id+"F2.wireOp",EDGE,"E6.22.1"),sQuery(id+"F2.wireOp",EDGE,"E6.22.2"),sQuery(id+"F2.wireOp",EDGE,"E6.23.0"),sQuery(id+"F2.wireOp",EDGE,"E6.23.1"),sQuery(id+"F2.wireOp",EDGE,"E6.23.2"),sQuery(id+"F2.wireOp",EDGE,"E6.24.0"),sQuery(id+"F2.wireOp",EDGE,"E6.24.1"),sQuery(id+"F2.wireOp",EDGE,"E6.24.2"),sQuery(id+"F2.wireOp",EDGE,"E6.25.0"),sQuery(id+"F2.wireOp",EDGE,"E6.25.1"),sQuery(id+"F2.wireOp",EDGE,"E6.25.2"),sQuery(id+"F2.wireOp",EDGE,"E6.26.0"),sQuery(id+"F2.wireOp",EDGE,"E6.26.1"),sQuery(id+"F2.wireOp",EDGE,"E6.26.2"),sQuery(id+"F2.wireOp",EDGE,"E6.27.0"),sQuery(id+"F2.wireOp",EDGE,"E6.27.1"),sQuery(id+"F2.wireOp",EDGE,"E6.27.2"),sQuery(id+"F2.wireOp",EDGE,"E6.28.0"),sQuery(id+"F2.wireOp",EDGE,"E6.28.1"),sQuery(id+"F2.wireOp",EDGE,"E6.28.2"),sQuery(id+"F2.wireOp",EDGE,"E6.29.0"),sQuery(id+"F2.wireOp",EDGE,"E6.29.1"),sQuery(id+"F2.wireOp",EDGE,"E6.29.2"),sQuery(id+"F2.wireOp",EDGE,"E6.30.0"),sQuery(id+"F2.wireOp",EDGE,"E6.30.1"),sQuery(id+"F2.wireOp",EDGE,"E6.30.2"),sQuery(id+"F2.wireOp",EDGE,"E6.31.0"),sQuery(id+"F2.wireOp",EDGE,"E6.31.1"),sQuery(id+"F2.wireOp",EDGE,"E6.31.2"),sQuery(id+"F2.wireOp",EDGE,"E6.32.0"),sQuery(id+"F2.wireOp",EDGE,"E6.32.1"),sQuery(id+"F2.wireOp",EDGE,"E6.32.2"),sQuery(id+"F2.wireOp",EDGE,"E6.33.0"),sQuery(id+"F2.wireOp",EDGE,"E6.33.1"),sQuery(id+"F2.wireOp",EDGE,"E6.33.2"),sQuery(id+"F2.wireOp",EDGE,"E6.34.0"),sQuery(id+"F2.wireOp",EDGE,"E6.34.1"),sQuery(id+"F2.wireOp",EDGE,"E6.34.2"),sQuery(id+"F2.wireOp",EDGE,"E6.35.0"),sQuery(id+"F2.wireOp",EDGE,"E6.35.1"),sQuery(id+"F2.wireOp",EDGE,"E6.35.2"),sQuery(id+"F2.wireOp",EDGE,"E6.36.0"),sQuery(id+"F2.wireOp",EDGE,"E6.36.1"),sQuery(id+"F2.wireOp",EDGE,"E6.36.2"),sQuery(id+"F2.wireOp",EDGE,"E6.37.0"),sQuery(id+"F2.wireOp",EDGE,"E6.37.1"),sQuery(id+"F2.wireOp",EDGE,"E6.37.2"),sQuery(id+"F2.wireOp",EDGE,"E6.38.0"),sQuery(id+"F2.wireOp",EDGE,"E6.38.1"),sQuery(id+"F2.wireOp",EDGE,"E6.38.2"),sQuery(id+"F2.wireOp",EDGE,"E6.39.0"),sQuery(id+"F2.wireOp",EDGE,"E6.39.1"),sQuery(id+"F2.wireOp",EDGE,"E6.39.2"),sQuery(id+"F2.wireOp",EDGE,"E6.40.0"),sQuery(id+"F2.wireOp",EDGE,"E6.40.1"),sQuery(id+"F2.wireOp",EDGE,"E6.40.2"),sQuery(id+"F2.wireOp",EDGE,"E6.41.0"),sQuery(id+"F2.wireOp",EDGE,"E6.41.1"),sQuery(id+"F2.wireOp",EDGE,"E6.41.2"),sQuery(id+"F2.wireOp",EDGE,"E6.42.0"),sQuery(id+"F2.wireOp",EDGE,"E6.42.1"),sQuery(id+"F2.wireOp",EDGE,"E6.42.2"),sQuery(id+"F2.wireOp",EDGE,"E6.43.0"),sQuery(id+"F2.wireOp",EDGE,"E6.43.1"),sQuery(id+"F2.wireOp",EDGE,"E6.43.2"),sQuery(id+"F2.wireOp",EDGE,"E6.44.0"),sQuery(id+"F2.wireOp",EDGE,"E6.44.1"),sQuery(id+"F2.wireOp",EDGE,"E6.44.2"),sQuery(id+"F2.wireOp",EDGE,"E6.45.0"),sQuery(id+"F2.wireOp",EDGE,"E6.45.1"),sQuery(id+"F2.wireOp",EDGE,"E6.45.2"),sQuery(id+"F2.wireOp",EDGE,"E6.46.0"),sQuery(id+"F2.wireOp",EDGE,"E6.46.1"),sQuery(id+"F2.wireOp",EDGE,"E6.46.2"),sQuery(id+"F2.wireOp",EDGE,"E6.47.0"),sQuery(id+"F2.wireOp",EDGE,"E6.47.1"),sQuery(id+"F2.wireOp",EDGE,"E6.47.2"),sQuery(id+"F2.wireOp",EDGE,"E6.48.0"),sQuery(id+"F2.wireOp",EDGE,"E6.48.1"),sQuery(id+"F2.wireOp",EDGE,"E6.48.2"),sQuery(id+"F2.wireOp",EDGE,"E6.49.0"),sQuery(id+"F2.wireOp",EDGE,"E6.49.1"),sQuery(id+"F2.wireOp",EDGE,"E6.49.2"),sQuery(id+"F2.wireOp",EDGE,"E6.50.0"),sQuery(id+"F2.wireOp",EDGE,"E6.50.1"),sQuery(id+"F2.wireOp",EDGE,"E6.50.2"),sQuery(id+"F2.wireOp",EDGE,"E6.51.0"),sQuery(id+"F2.wireOp",EDGE,"E6.51.1"),sQuery(id+"F2.wireOp",EDGE,"E6.51.2"),sQuery(id+"F2.wireOp",EDGE,"E6.52.0"),sQuery(id+"F2.wireOp",EDGE,"E6.52.1"),sQuery(id+"F2.wireOp",EDGE,"E6.52.2"),sQuery(id+"F2.wireOp",EDGE,"E6.53.0"),sQuery(id+"F2.wireOp",EDGE,"E6.53.1"),sQuery(id+"F2.wireOp",EDGE,"E6.53.2"),sQuery(id+"F2.wireOp",EDGE,"E6.54.0"),sQuery(id+"F2.wireOp",EDGE,"E6.54.1"),sQuery(id+"F2.wireOp",EDGE,"E6.54.2"),sQuery(id+"F2.wireOp",EDGE,"E6.55.0"),sQuery(id+"F2.wireOp",EDGE,"E6.55.1"),sQuery(id+"F2.wireOp",EDGE,"E6.55.2"),sQuery(id+"F2.wireOp",EDGE,"E6.56.0"),sQuery(id+"F2.wireOp",EDGE,"E6.56.1"),sQuery(id+"F2.wireOp",EDGE,"E6.56.2"),sQuery(id+"F2.wireOp",EDGE,"E6.57.0"),sQuery(id+"F2.wireOp",EDGE,"E6.57.1"),sQuery(id+"F2.wireOp",EDGE,"E6.57.2"),sQuery(id+"F2.wireOp",EDGE,"E6.58.0"),sQuery(id+"F2.wireOp",EDGE,"E6.58.1"),sQuery(id+"F2.wireOp",EDGE,"E6.58.2"),sQuery(id+"F2.wireOp",EDGE,"E6.59.0"),sQuery(id+"F2.wireOp",EDGE,"E6.59.1"),sQuery(id+"F2.wireOp",EDGE,"E6.59.2"),sQuery(id+"F2.wireOp",EDGE,"E6.60.0"),sQuery(id+"F2.wireOp",EDGE,"E6.60.1"),sQuery(id+"F2.wireOp",EDGE,"E6.60.2"),sQuery(id+"F2.wireOp",EDGE,"E6.61.0"),sQuery(id+"F2.wireOp",EDGE,"E6.61.1"),sQuery(id+"F2.wireOp",EDGE,"E6.61.2"),sQuery(id+"F2.wireOp",EDGE,"E6.62.0"),sQuery(id+"F2.wireOp",EDGE,"E6.62.1"),sQuery(id+"F2.wireOp",EDGE,"E6.62.2"),sQuery(id+"F2.wireOp",EDGE,"E6.63.0"),sQuery(id+"F2.wireOp",EDGE,"E6.63.1"),sQuery(id+"F2.wireOp",EDGE,"E6.63.2"),sQuery(id+"F2.wireOp",EDGE,"E6.64.0"),sQuery(id+"F2.wireOp",EDGE,"E6.64.1"),sQuery(id+"F2.wireOp",EDGE,"E6.64.2"),sQuery(id+"F2.wireOp",EDGE,"E6.65.0"),sQuery(id+"F2.wireOp",EDGE,"E6.65.1"),sQuery(id+"F2.wireOp",EDGE,"E6.65.2"),sQuery(id+"F2.wireOp",EDGE,"E6.66.0"),sQuery(id+"F2.wireOp",EDGE,"E6.66.1"),sQuery(id+"F2.wireOp",EDGE,"E6.66.2"),sQuery(id+"F2.wireOp",EDGE,"E6.67.0"),sQuery(id+"F2.wireOp",EDGE,"E6.67.1"),sQuery(id+"F2.wireOp",EDGE,"E6.67.2"),sQuery(id+"F2.wireOp",EDGE,"E6.68.0"),sQuery(id+"F2.wireOp",EDGE,"E6.68.1"),sQuery(id+"F2.wireOp",EDGE,"E6.68.2"),sQuery(id+"F2.wireOp",EDGE,"E6.69.0"),sQuery(id+"F2.wireOp",EDGE,"E6.69.1"),sQuery(id+"F2.wireOp",EDGE,"E6.69.2"),sQuery(id+"F2.wireOp",EDGE,"E6.70.0"),sQuery(id+"F2.wireOp",EDGE,"E6.70.1"),sQuery(id+"F2.wireOp",EDGE,"E6.70.2"),sQuery(id+"F2.wireOp",EDGE,"E6.71.0"),sQuery(id+"F2.wireOp",EDGE,"E6.71.1"),sQuery(id+"F2.wireOp",EDGE,"E6.71.2"),sQuery(id+"F2.wireOp",EDGE,"E6.72.0"),sQuery(id+"F2.wireOp",EDGE,"E6.72.1"),sQuery(id+"F2.wireOp",EDGE,"E6.72.2"),sQuery(id+"F2.wireOp",EDGE,"E6.73.0"),sQuery(id+"F2.wireOp",EDGE,"E6.73.1"),sQuery(id+"F2.wireOp",EDGE,"E6.73.2"),sQuery(id+"F2.wireOp",EDGE,"E6.74.0"),sQuery(id+"F2.wireOp",EDGE,"E6.74.1"),sQuery(id+"F2.wireOp",EDGE,"E6.74.2"),sQuery(id+"F2.wireOp",EDGE,"E6.75.0"),sQuery(id+"F2.wireOp",EDGE,"E6.75.1"),sQuery(id+"F2.wireOp",EDGE,"E6.75.2"),sQuery(id+"F2.wireOp",EDGE,"E6.76.0"),sQuery(id+"F2.wireOp",EDGE,"E6.76.1"),sQuery(id+"F2.wireOp",EDGE,"E6.76.2"),sQuery(id+"F2.wireOp",EDGE,"E6.77.0"),sQuery(id+"F2.wireOp",EDGE,"E6.77.1"),sQuery(id+"F2.wireOp",EDGE,"E6.77.2"),sQuery(id+"F2.wireOp",EDGE,"E6.78.0"),sQuery(id+"F2.wireOp",EDGE,"E6.78.1"),sQuery(id+"F2.wireOp",EDGE,"E6.78.2"),sQuery(id+"F2.wireOp",EDGE,"E6.79.0"),sQuery(id+"F2.wireOp",EDGE,"E6.79.1"),sQuery(id+"F2.wireOp",EDGE,"E6.79.2")])],"isStart":false});
            var sketch = newSketch(context, id + "F4", { "sketchPlane" : qUnion([Q0])});
            skCircle(sketch, "E7", {"center": v(0, 0) * mm, "radius": 19.05 * mm});
            skSolve(sketch);
        }
        {
            var Q0;
            Q0 = qSketchRegion(id + "F4", true);
            extrude(context, id + "F5", {"entities" : qUnion([Q0]), "operationType" : NewBodyOperationType.ADD, "depth" : 12.7 * mm, "offsetDistance" : 25.4 * mm});
        }
        {
            var Q0;
            Q0=makeQuery(id+"F5.opExtrude","CAP_FACE",FACE,{"disambiguationData":[OSD([sQuery(id+"F4.wireOp",EDGE,"E7")])],"isStart":false});
            var sketch = newSketch(context, id + "F6", { "sketchPlane" : qUnion([Q0])});
            skCircle(sketch, "E8.cCircle", {"center": v(0, 0) * mm, "radius": 5.46 * mm, "construction": true});
            skLineSegment(sketch, "E8.0", {"start": v(3.27, 5.4) * mm, "end": v(6.3, -0.14) * mm});
            skLineSegment(sketch, "E8.1", {"start": v(6.3, -0.14) * mm, "end": v(3.03, -5.53) * mm});
            skLineSegment(sketch, "E8.2", {"start": v(3.03, -5.53) * mm, "end": v(-3.27, -5.4) * mm});
            skLineSegment(sketch, "E8.3", {"start": v(-3.27, -5.4) * mm, "end": v(-6.3, 0.14) * mm});
            skLineSegment(sketch, "E8.4", {"start": v(-6.3, 0.14) * mm, "end": v(-3.03, 5.53) * mm});
            skLineSegment(sketch, "E8.5", {"start": v(-3.03, 5.53) * mm, "end": v(3.27, 5.4) * mm});
            skPoint(sketch, "E8.0.midPoint", {"position": v(4.79, 2.63) * mm});
            skSolve(sketch);
        }
        {
            var Q0;
            Q0 = qSketchRegion(id + "F6", true);
            extrude(context, id + "F7", {"entities" : qUnion([Q0]), "operationType" : NewBodyOperationType.ADD, "depth" : 6.35 * mm, "offsetDistance" : 25.4 * mm});
        }
        {
            var Q0;
            Q0=makeQuery(id+"F7.opExtrude","CAP_FACE",FACE,{"disambiguationData":[OSD([sQuery(id+"F6.wireOp",EDGE,"E8.0"),sQuery(id+"F6.wireOp",EDGE,"E8.1"),sQuery(id+"F6.wireOp",EDGE,"E8.2"),sQuery(id+"F6.wireOp",EDGE,"E8.3"),sQuery(id+"F6.wireOp",EDGE,"E8.4"),sQuery(id+"F6.wireOp",EDGE,"E8.5")])],"isStart":false});
            var sketch = newSketch(context, id + "F8", { "sketchPlane" : qUnion([Q0])});
            skCircle(sketch, "E9", {"center": v(0, 0) * mm, "radius": 3.81 * mm});
            skSolve(sketch);
        }
        {
            var Q0;
            Q0 = qSketchRegion(id + "F8", true);
            extrude(context, id + "F9", {"entities" : qUnion([Q0]), "operationType" : NewBodyOperationType.REMOVE, "oppositeDirection" : true, "depth" : 30.73 * mm, "offsetDistance" : 25.4 * mm});
        }
        {
            var Q0;
            Q0=makeQuery(id+"F1.opExtrude","CAP_FACE",FACE,{"disambiguationData":[OSD([sQuery(id+"F0.wireOp",EDGE,"E0")])],"isStart":true});
            var sketch = newSketch(context, id + "F10", { "sketchPlane" : qUnion([Q0])});
            skCircle(sketch, "E10", {"center": v(0, 0) * mm, "radius": 8 * mm});
            skSolve(sketch);
        }
        {
            var Q0;
            Q0 = qSketchRegion(id + "F10", true);
            extrude(context, id + "F11", {"entities" : qUnion([Q0]), "operationType" : NewBodyOperationType.REMOVE, "oppositeDirection" : true, "depth" : 17.78 * mm, "offsetDistance" : 25.4 * mm});
        }
    });
